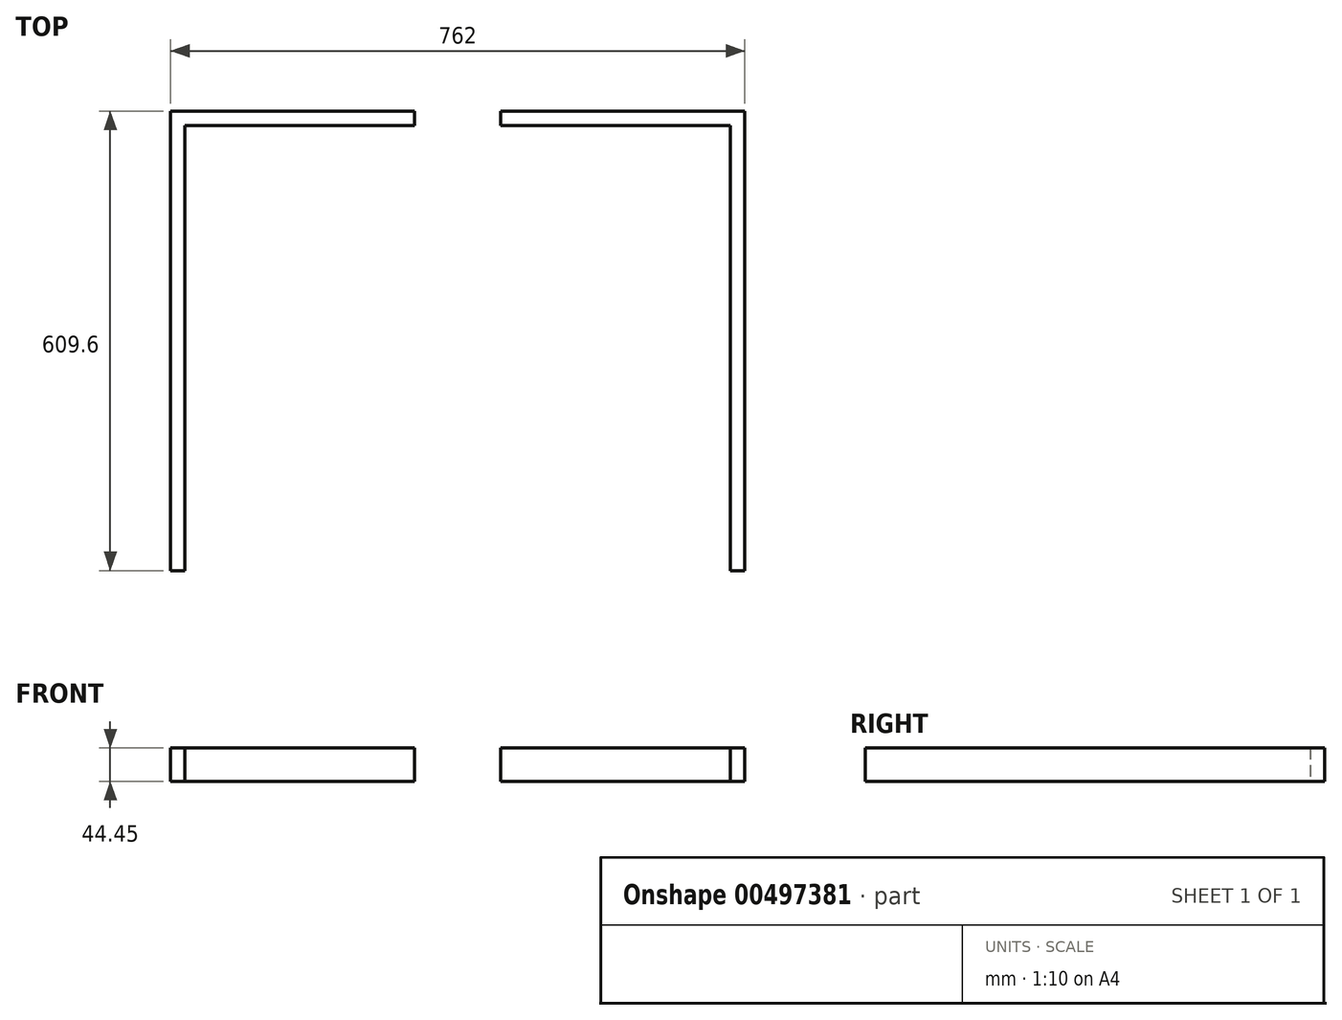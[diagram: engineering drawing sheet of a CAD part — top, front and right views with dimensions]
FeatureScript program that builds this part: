
annotation { "Feature Type Name" : "Feature", "Feature Type Description" : "" }
export const myFeature = defineFeature(function(context is Context, id is Id, definition is map)
    precondition{}
    {
        {
            var Q0;
            Q0=qCreatedBy(makeId("Top.planeOp"),FACE);
            var sketch = newSketch(context, id + "F0", { "sketchPlane" : qUnion([Q0])});
            skLineSegment(sketch, "E0", {"start": v(-361.95, -609.6) * mm, "end": v(-381, -609.6) * mm});
            skLineSegment(sketch, "E1", {"start": v(-381, -609.6) * mm, "end": v(-381, 0) * mm});
            skLineSegment(sketch, "E2", {"start": v(-381, 0) * mm, "end": v(-57.15, 0) * mm});
            skLineSegment(sketch, "E3", {"start": v(-57.15, 0) * mm, "end": v(-57.15, -19.05) * mm});
            skLineSegment(sketch, "E4", {"start": v(-57.15, -19.05) * mm, "end": v(-361.95, -19.05) * mm});
            skLineSegment(sketch, "E5", {"start": v(-361.95, -19.05) * mm, "end": v(-361.95, -609.6) * mm});
            skLineSegment(sketch, "E6", {"start": v(57.15, 0) * mm, "end": v(381, 0) * mm});
            skLineSegment(sketch, "E7", {"start": v(381, 0) * mm, "end": v(381, -609.6) * mm});
            skLineSegment(sketch, "E8", {"start": v(381, -609.6) * mm, "end": v(361.95, -609.6) * mm});
            skLineSegment(sketch, "E9", {"start": v(361.95, -609.6) * mm, "end": v(361.95, -19.05) * mm});
            skLineSegment(sketch, "E10", {"start": v(361.95, -19.05) * mm, "end": v(57.15, -19.05) * mm});
            skLineSegment(sketch, "E11", {"start": v(57.15, -19.05) * mm, "end": v(57.15, 0) * mm});
            skSolve(sketch);
        }
        {
            var Q0;
            Q0 = qSketchRegion(id + "F0", true);
            extrude(context, id + "F1", {"entities" : qUnion([Q0]), "depth" : 44.45 * mm});
        }
    });
